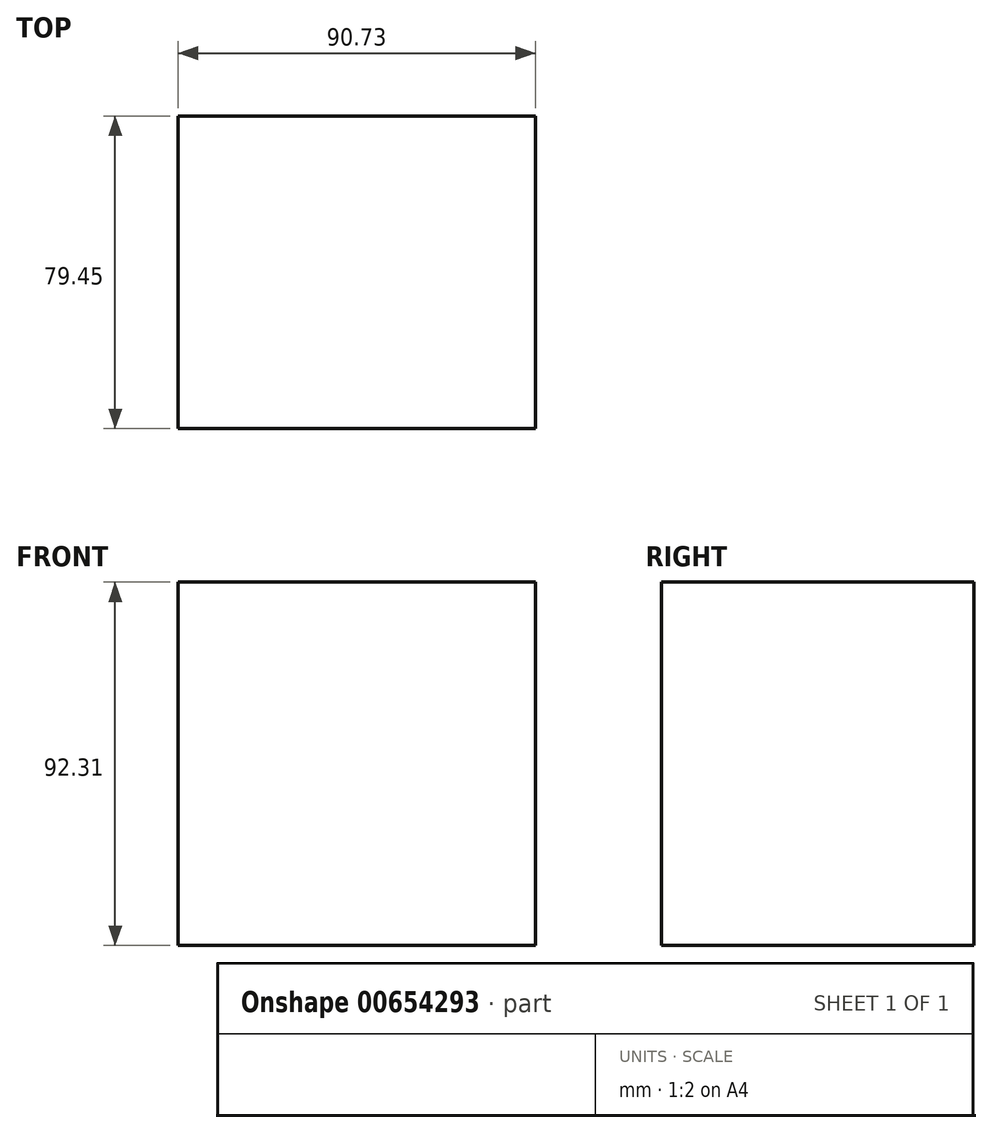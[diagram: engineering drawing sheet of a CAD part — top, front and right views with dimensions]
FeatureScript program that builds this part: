
annotation { "Feature Type Name" : "Feature", "Feature Type Description" : "" }
export const myFeature = defineFeature(function(context is Context, id is Id, definition is map)
    precondition{}
    {
        {
            var Q0;
            Q0=qCreatedBy(makeId("Top.planeOp"),FACE);
            var sketch = newSketch(context, id + "F0", { "sketchPlane" : qUnion([Q0])});
            skLineSegment(sketch, "E0.bottom", {"start": v(0, 40.36) * mm, "end": v(0, 40.36) * mm});
            skLineSegment(sketch, "E0.top", {"start": v(0, 42.19) * mm, "end": v(0, 42.19) * mm});
            skLineSegment(sketch, "E0.left", {"start": v(0, 40.36) * mm, "end": v(0, 42.19) * mm});
            skLineSegment(sketch, "E0.right", {"start": v(0, 40.36) * mm, "end": v(0, 42.19) * mm});
            skLineSegment(sketch, "E1.bottom", {"start": v(15.87, -39.1) * mm, "end": v(106.6, -39.1) * mm});
            skLineSegment(sketch, "E1.top", {"start": v(15.87, 40.36) * mm, "end": v(106.6, 40.36) * mm});
            skLineSegment(sketch, "E1.left", {"start": v(15.87, -39.1) * mm, "end": v(15.87, 40.36) * mm});
            skLineSegment(sketch, "E1.right", {"start": v(106.6, -39.1) * mm, "end": v(106.6, 40.36) * mm});
            skSolve(sketch);
        }
        {
            var Q0;
            Q0=makeQuery(id+"F0.imprint","IMPRINT",FACE,{"disambiguationData":[TD([[makeQuery(id+"F0.imprint","IMPRINT",EDGE,{"derivedFrom":sQuery(id+"F0.wireOp",EDGE,"E1.bottom")}),1.0]])]});
            extrude(context, id + "F1", {"entities" : qUnion([Q0]), "depth" : 92.3 * mm, "offsetDistance" : 25.4 * mm});
        }
    });
